# Revit family: Electronics_Controllers_Biamp_Vocia_Wall-Remote_WR-1__
name_source: partatom
category: Communication Devices
units: mm (PartAtom-declared; Revit-internal decimal feet)

## family parameters
Cut with Voids When Loaded = Yes
Host = Face
Maintain Annotation Orientation = No
OmniClass Number = 23.85.10.11
OmniClass Title = Audio Information, Sound Signals
Part Type = Normal
Room Calculation Point = No
Round Connector Dimension = Use Diameter
Shared = No

## types (1)
- WR-1
    Altitude = 0-10,000 ft (0-3000m) MSL
    Apparent Load = 0 VA
    Compliance = CE marked (Europe), RoHS Directive (Europe)
    Connector Description = RJ-45; PoE 802.3af Class 1
    Default Elevation = 48 "
    Depth = 1.8 "
    Description = Vocia® WR-1 Wall Remote
    Height = 5.1 "
    Housing Material = Biamp - Plastic - White
    Humidity = 0-95% relative humidity (non-condensing)
    Manufacturer = Biamp
    Max Power Consumption = 0 W
    Model = Vocia WR-1
    Network Connection = RJ-45 with shielded Ethernet (CAT5, CAT5e, CAT6 or CAT7)
    Number of Poles = 1
    Power Factor = 1
    Product Documentation Link = https://downloads.biamp.com
    Product Page URL = https://www.biamp.com
    Product data url = https://www.bimobject.com
    Temperature Range = 23 - 104° F (-5 - 40° C)
    URL = https://www.biamp.com
    Voltage = 0 V
    Weight = 0.40 lbf
    Width = 6 "
    Within Wall Depth = 1.2 "
    Within Wall Width = 2.9 "
    Withit Wall Height = 2.4 "

## geometry (parser evidence)
native form markers: Sweep x2
no freeform markers — native parametric forms only
